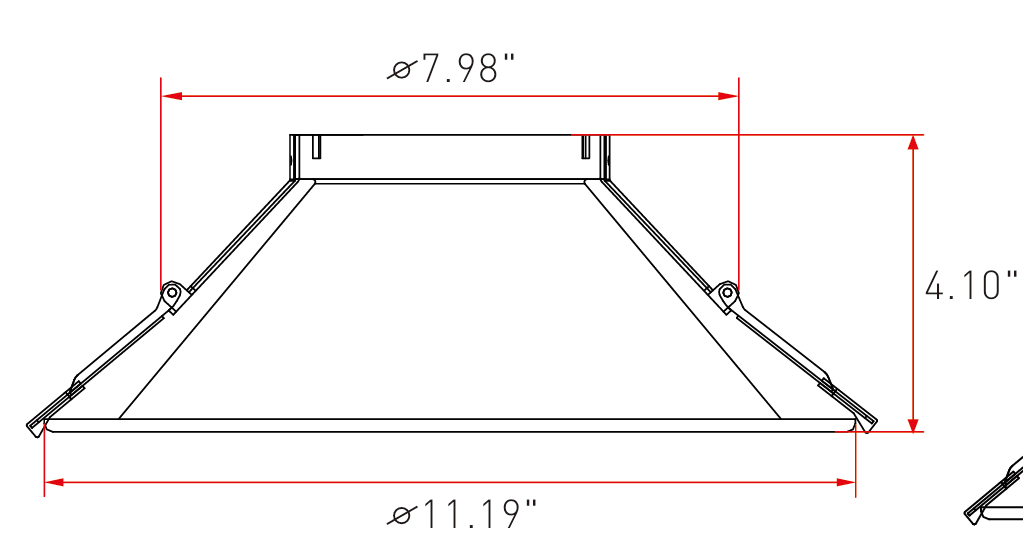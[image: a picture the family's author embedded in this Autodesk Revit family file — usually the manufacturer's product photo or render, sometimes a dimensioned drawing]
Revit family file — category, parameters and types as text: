
# Revit family: Alcon-14123-10R-Revit-Family
name_source: partatom
category: Lighting Fixtures
units: mm (PartAtom-declared; Revit-internal decimal feet)

## family parameters
Always vertical = Yes
Cut with Voids When Loaded = No
Host = Ceiling
Light Source = Yes
OmniClass Number = 23.80.70.11
OmniClass Title = Luminaries for Internal Lighting
Part Type = Normal
Room Calculation Point = No
Round Connector Dimension = Use Diameter
Shared = No

## types (1)
- Type 1
    Color Filter = 16777215
    Default Elevation = 0' - 0"
    Dimming Lamp Color Temperature Shift = <None>
    Housing = <By Category>
    Light Source Symbol Length = 10' - 0"
    LightSource = <By Category>
    Link To Product Page = https://www.alconlighting.com
    Manufacturer = Alcon Light
    Product Identity = Alcon Lighting 14123-10R
    Spot Beam Angle = 30.00°
    Spot Field Angle = 90.00°
    Tilt Angle = 60.00°

## geometry (parser evidence)
native form markers: Sweep x2
no freeform markers — native parametric forms only
